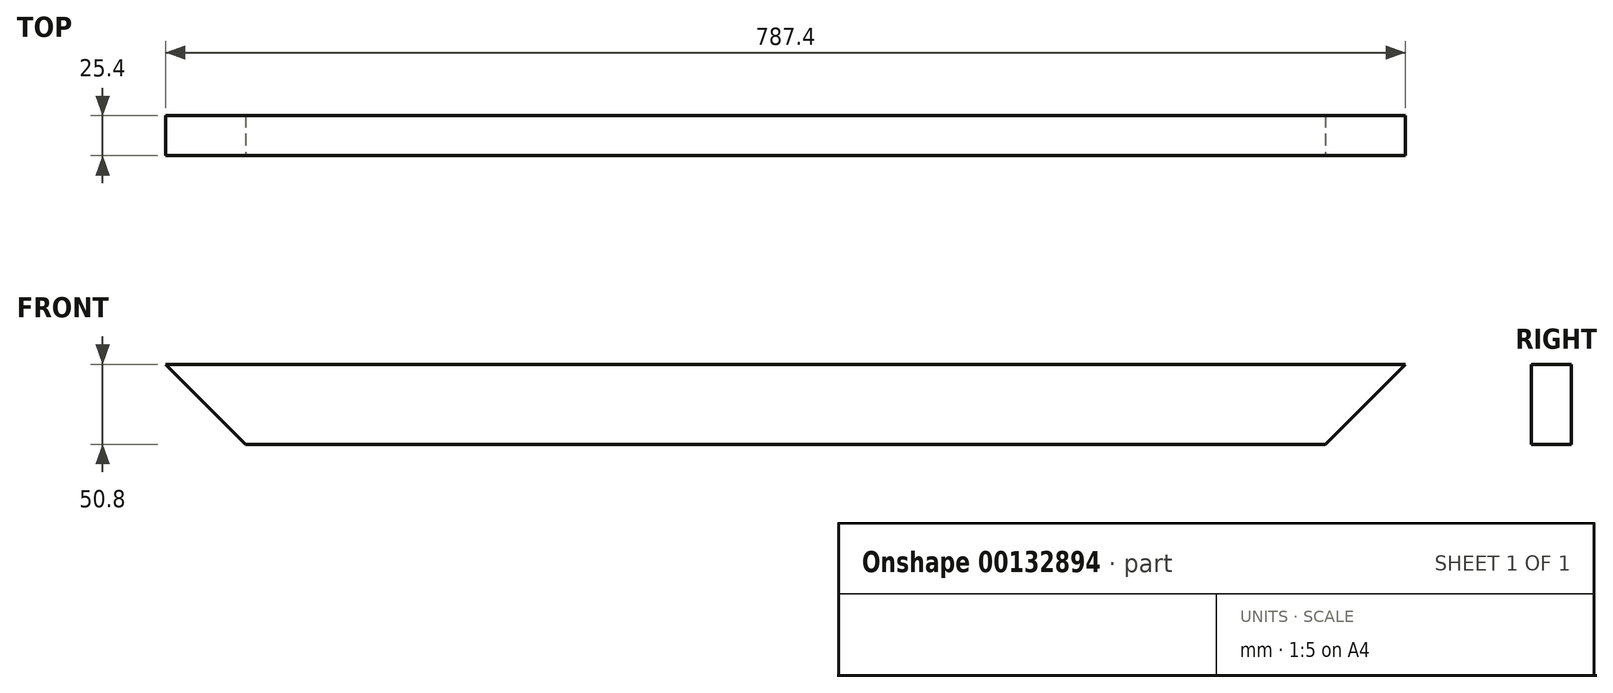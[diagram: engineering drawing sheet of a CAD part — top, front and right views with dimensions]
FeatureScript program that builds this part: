
annotation { "Feature Type Name" : "Feature", "Feature Type Description" : "" }
export const myFeature = defineFeature(function(context is Context, id is Id, definition is map)
    precondition{}
    {
        {
            var Q0;
            Q0=qCreatedBy(makeId("Front.planeOp"),FACE);
            var sketch = newSketch(context, id + "F0", { "sketchPlane" : qUnion([Q0])});
            skLineSegment(sketch, "E0.bottom", {"start": v(233.23, -111.87) * mm, "end": v(-554.17, -111.87) * mm});
            skLineSegment(sketch, "E0.top", {"start": v(233.23, -61.07) * mm, "end": v(-554.17, -61.07) * mm});
            skLineSegment(sketch, "E0.left", {"start": v(233.23, -111.87) * mm, "end": v(233.23, -61.07) * mm});
            skLineSegment(sketch, "E0.right", {"start": v(-554.17, -111.87) * mm, "end": v(-554.17, -61.07) * mm});
            skPoint(sketch, "E0.middle", {"position": v(-160.47, -86.47) * mm});
            skSolve(sketch);
        }
        {
            var Q0;
            Q0 = qSketchRegion(id + "F0", true);
            extrude(context, id + "F1", {"entities" : qUnion([Q0]), "depth" : 25.4 * mm});
        }
        {
            var Q0;
            Q0=makeQuery(id+"F1.opExtrude","CAP_FACE",FACE,{"disambiguationData":[OSD([sQuery(id+"F0.wireOp",EDGE,"E0.bottom"),sQuery(id+"F0.wireOp",EDGE,"E0.top"),sQuery(id+"F0.wireOp",EDGE,"E0.left"),sQuery(id+"F0.wireOp",EDGE,"E0.right")])],"isStart":false});
            var sketch = newSketch(context, id + "F2", { "sketchPlane" : qUnion([Q0])});
            skLineSegment(sketch, "E1.top", {"start": v(233.23, -111.87) * mm, "end": v(182.43, -111.87) * mm});
            skLineSegment(sketch, "E1.left", {"start": v(233.23, -61.07) * mm, "end": v(233.23, -111.87) * mm});
            skLineSegment(sketch, "E2", {"start": v(233.23, -61.07) * mm, "end": v(182.43, -111.87) * mm});
            skSolve(sketch);
        }
        {
            var Q0;
            Q0=makeQuery(id+"F2.imprint","IMPRINT",FACE,{"disambiguationData":[TD([[makeQuery(id+"F2.imprint","IMPRINT",EDGE,{"derivedFrom":sQuery(id+"F2.wireOp",EDGE,"E1.top")}),-1.0]])]});
            extrude(context, id + "F3", {"entities" : qUnion([Q0]), "operationType" : NewBodyOperationType.REMOVE, "oppositeDirection" : true, "depth" : 25.4 * mm});
        }
        {
            var Q0;
            Q0=makeQuery(id+"F1.opExtrude","CAP_FACE",FACE,{"disambiguationData":[OSD([sQuery(id+"F0.wireOp",EDGE,"E0.bottom"),sQuery(id+"F0.wireOp",EDGE,"E0.top"),sQuery(id+"F0.wireOp",EDGE,"E0.left"),sQuery(id+"F0.wireOp",EDGE,"E0.right")])],"isStart":false});
            var sketch = newSketch(context, id + "F4", { "sketchPlane" : qUnion([Q0])});
            skLineSegment(sketch, "E3.top", {"start": v(-554.17, -111.87) * mm, "end": v(-503.37, -111.87) * mm});
            skLineSegment(sketch, "E3.left", {"start": v(-554.17, -61.07) * mm, "end": v(-554.17, -111.87) * mm});
            skLineSegment(sketch, "E4", {"start": v(-554.17, -61.07) * mm, "end": v(-503.37, -111.87) * mm});
            skSolve(sketch);
        }
        {
            var Q0;
            Q0=makeQuery(id+"F4.imprint","IMPRINT",FACE,{"disambiguationData":[TD([[makeQuery(id+"F4.imprint","IMPRINT",EDGE,{"derivedFrom":sQuery(id+"F4.wireOp",EDGE,"E3.top")}),-1.0]])]});
            extrude(context, id + "F5", {"entities" : qUnion([Q0]), "operationType" : NewBodyOperationType.REMOVE, "oppositeDirection" : true, "depth" : 25.4 * mm});
        }
    });
